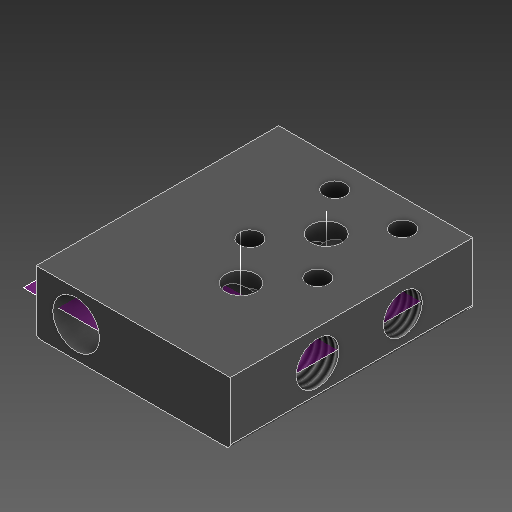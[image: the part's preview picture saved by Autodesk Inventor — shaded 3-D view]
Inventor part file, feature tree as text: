
AUTODESK INVENTOR PART (.ipt)
format: ipt  version: 2021 (Build 250183000, 183)  size: 232,960 bytes
history: native  units: in
note: dims shown in document units (in); Inventor stores cm internally (conversion verified against a paired STEP export)
features: other x6, sketch x4, plane x3
ambient origin geometry x8: Origin, YZ Plane, XZ Plane, XY Plane, X Axis, Y Axis, Z Axis, Center Point
bodies: Solid1 (feature_tree)
feature tree (13):
  other  "Val_BodV4.ipt"
  other  "Solid1::Val_BodV4.ipt"
  other  "TaggingFeature1"
  sketch  "Sketch3"  dims[d0=0.3937in]
  sketch  "Sketch5"
  sketch  "Sketch6"
  sketch  "Sketch4"
  plane  "Work Plane1"
  plane  "Work Plane2"
  plane  "Work Plane3"
  other  "Work Axis1"
  other  "Work Axis2"
  other  "Work Axis3"
